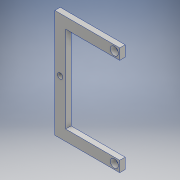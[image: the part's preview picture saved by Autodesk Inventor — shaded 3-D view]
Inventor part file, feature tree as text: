
AUTODESK INVENTOR PART (.ipt)
format: ipt  version: 2018.1 (Build 221171000, 171)  size: 122,368 bytes
history: native  units: mm
features: extrude x2, sketch x2, other x1
ambient origin geometry x8: Origin, YZ Plane, XZ Plane, XY Plane, X Axis, Y Axis, Z Axis, Center Point
bodies: Body1 (feature_tree)
feature tree (5):
  other  "ソリッド1"
  extrude  "押し出し1"  Depth=10.0mm
  extrude  "押し出し2"  Depth=50.0mm
  sketch  "スケッチ1"
  sketch  "スケッチ2"
